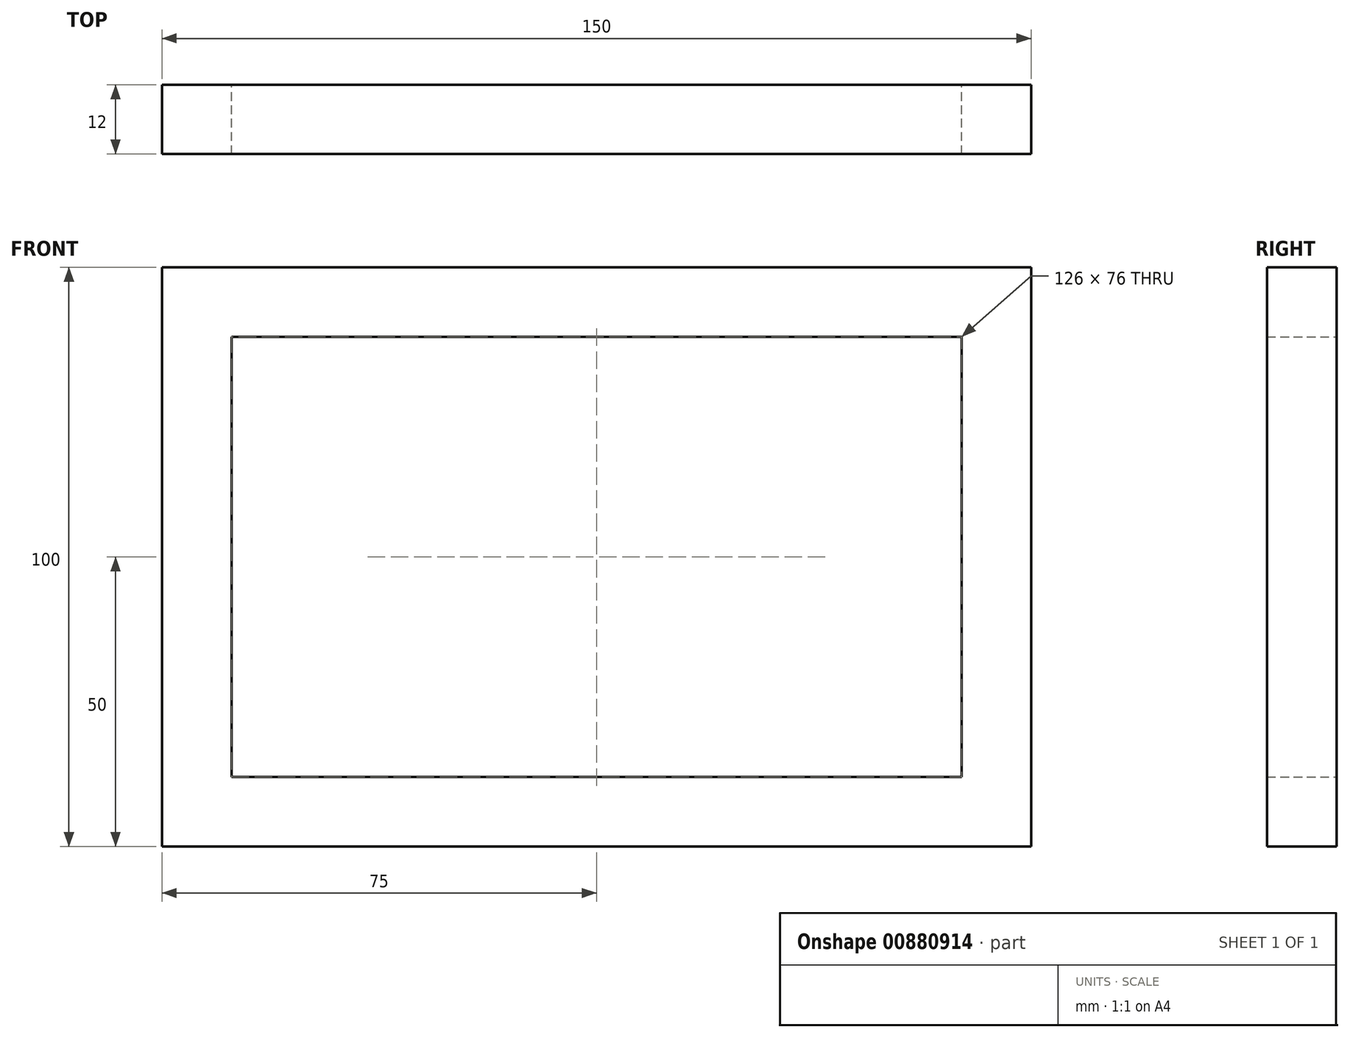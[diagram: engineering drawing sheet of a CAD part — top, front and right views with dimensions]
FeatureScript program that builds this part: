
annotation { "Feature Type Name" : "Feature", "Feature Type Description" : "" }
export const myFeature = defineFeature(function(context is Context, id is Id, definition is map)
    precondition{}
    {
        {
            var Q0;
            Q0=qCreatedBy(makeId("Front.planeOp"),FACE);
            var sketch = newSketch(context, id + "F0", { "sketchPlane" : qUnion([Q0])});
            skLineSegment(sketch, "E0.bottom", {"start": v(-75, 50) * mm, "end": v(75, 50) * mm});
            skLineSegment(sketch, "E0.top", {"start": v(-75, -50) * mm, "end": v(75, -50) * mm});
            skLineSegment(sketch, "E0.left", {"start": v(-75, 50) * mm, "end": v(-75, -50) * mm});
            skLineSegment(sketch, "E0.right", {"start": v(75, 50) * mm, "end": v(75, -50) * mm});
            skPoint(sketch, "E0.middle", {"position": v(0, 0) * mm});
            skLineSegment(sketch, "E1", {"start": v(-63, -38) * mm, "end": v(-63, 38) * mm});
            skLineSegment(sketch, "E2", {"start": v(-63, 38) * mm, "end": v(0, 38) * mm});
            skLineSegment(sketch, "E3", {"start": v(0, 38) * mm, "end": v(63, 38) * mm});
            skLineSegment(sketch, "E4", {"start": v(63, 38) * mm, "end": v(63, -38) * mm});
            skLineSegment(sketch, "E5", {"start": v(63, -38) * mm, "end": v(0, -38) * mm});
            skLineSegment(sketch, "E6", {"start": v(0, -38) * mm, "end": v(-63, -38) * mm});
            skLineSegment(sketch, "E7", {"start": v(0, 38) * mm, "end": v(0, -38) * mm});
            skLineSegment(sketch, "E8", {"start": v(-75, 50) * mm, "end": v(-63, 50) * mm});
            skSolve(sketch);
        }
        {
            var Q0;
            Q0 = qSketchRegion(id + "F0", true);
            extrude(context, id + "F1", {"entities" : qUnion([Q0]), "depth" : 12 * mm, "offsetDistance" : 25 * mm});
        }
    });
